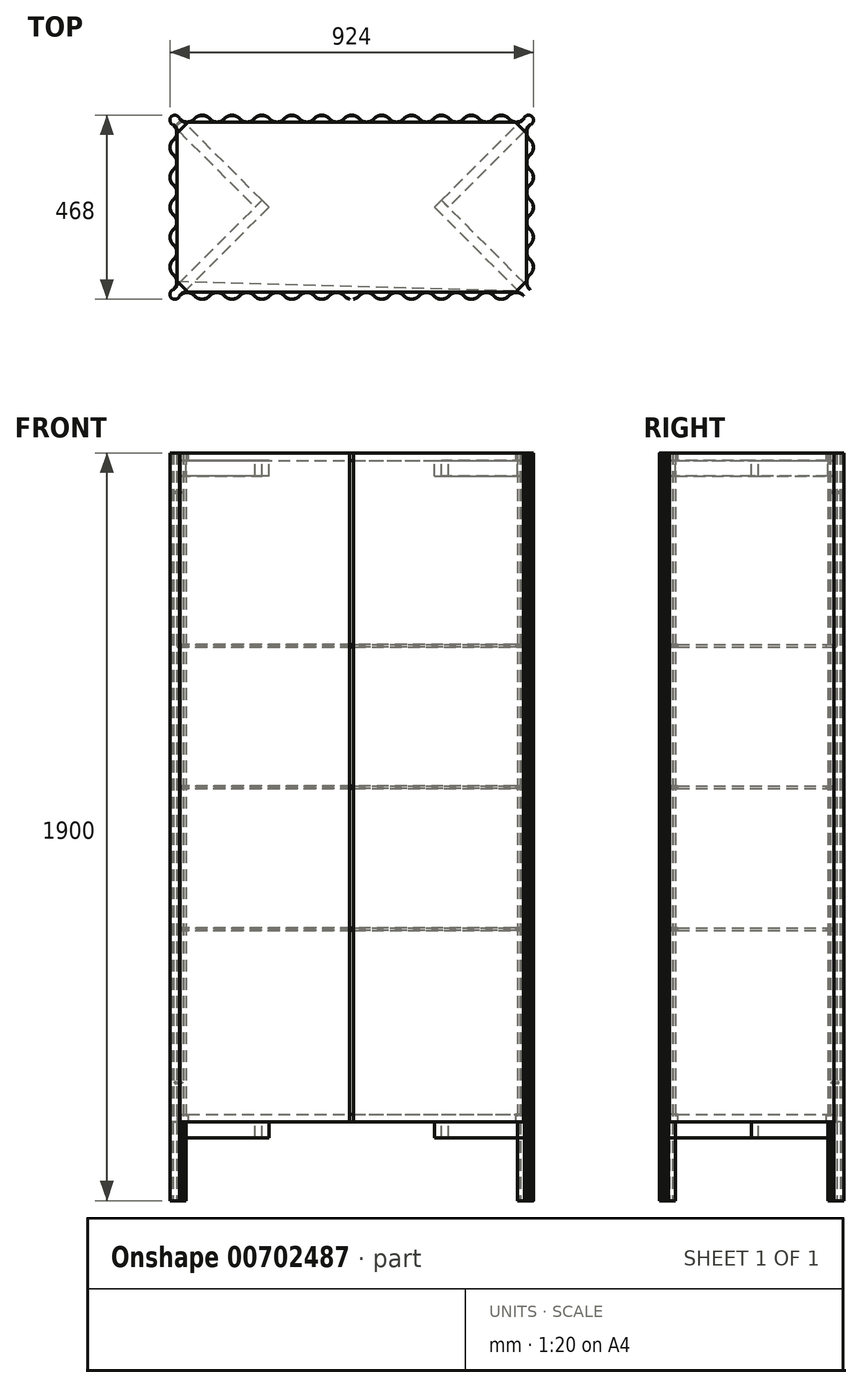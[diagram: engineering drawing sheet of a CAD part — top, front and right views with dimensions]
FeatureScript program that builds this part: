
annotation { "Feature Type Name" : "Feature", "Feature Type Description" : "" }
export const myFeature = defineFeature(function(context is Context, id is Id, definition is map)
    precondition{}
    {
        {
            var Q0;
            Q0=qCreatedBy(makeId("Top.planeOp"),FACE);
            var sketch = newSketch(context, id + "F0", { "sketchPlane" : qUnion([Q0])});
            skArc(sketch, "E0", {"start": v(19, 224.64) * mm, "mid": v(10.44, 231.03) * mm, "end": v(0, 233.3) * mm});
            skArc(sketch, "E1", {"start": v(19, 224.64) * mm, "mid": v(27.56, 218.26) * mm, "end": v(38, 216) * mm});
            skLineSegment(sketch, "E2", {"start": v(0, 285.6) * mm, "end": v(0, 208.1) * mm, "construction": true});
            skArc(sketch, "E3.1", {"start": v(19.53, 225.1) * mm, "mid": v(10.73, 231.66) * mm, "end": v(0, 234) * mm});
            skArc(sketch, "E3.2", {"start": v(19.53, 225.1) * mm, "mid": v(27.85, 218.9) * mm, "end": v(38, 216.7) * mm});
            skLineSegment(sketch, "E4", {"start": v(-82.64, 234) * mm, "end": v(38, 234) * mm, "construction": true});
            skLineSegment(sketch, "E5", {"start": v(-38, 216) * mm, "end": v(38, 216) * mm, "construction": true});
            skLineSegment(sketch, "E6", {"start": v(465.57, 237.57) * mm, "end": v(228, 0) * mm, "construction": true});
            skLineSegment(sketch, "E7.bottom", {"start": v(440.65, 230.33) * mm, "end": v(437.4, 227.07) * mm});
            skLineSegment(sketch, "E7.right", {"start": v(421.2, 210.88) * mm, "end": v(438.88, 193.2) * mm});
            skArc(sketch, "E8", {"start": v(458.33, 212.65) * mm, "mid": v(458.33, 230.33) * mm, "end": v(440.65, 230.33) * mm});
            skArc(sketch, "E9.1.0.0", {"start": v(95, 224.64) * mm, "mid": v(103.56, 218.26) * mm, "end": v(114, 216) * mm});
            skArc(sketch, "E9.1.0.1", {"start": v(57, 224.64) * mm, "mid": v(48.44, 218.26) * mm, "end": v(38, 216) * mm});
            skArc(sketch, "E9.1.0.2", {"start": v(56.47, 225.1) * mm, "mid": v(48.15, 218.9) * mm, "end": v(38, 216.7) * mm});
            skArc(sketch, "E9.1.0.3", {"start": v(95.53, 225.1) * mm, "mid": v(76, 234) * mm, "end": v(56.47, 225.1) * mm});
            skLineSegment(sketch, "E9.1.0.4", {"start": v(38, 216) * mm, "end": v(114, 216) * mm, "construction": true});
            skLineSegment(sketch, "E9.1.0.5", {"start": v(-6.64, 234) * mm, "end": v(114, 234) * mm, "construction": true});
            skArc(sketch, "E9.1.0.6", {"start": v(95.53, 225.1) * mm, "mid": v(103.85, 218.9) * mm, "end": v(114, 216.7) * mm});
            skArc(sketch, "E9.1.0.7", {"start": v(95, 224.64) * mm, "mid": v(76, 233.3) * mm, "end": v(57, 224.64) * mm});
            skArc(sketch, "E9.2.0.0", {"start": v(171, 224.64) * mm, "mid": v(179.56, 218.26) * mm, "end": v(190, 216) * mm});
            skArc(sketch, "E9.2.0.1", {"start": v(133, 224.64) * mm, "mid": v(124.44, 218.26) * mm, "end": v(114, 216) * mm});
            skArc(sketch, "E9.2.0.2", {"start": v(132.47, 225.1) * mm, "mid": v(124.15, 218.9) * mm, "end": v(114, 216.7) * mm});
            skArc(sketch, "E9.2.0.3", {"start": v(171.53, 225.1) * mm, "mid": v(152, 234) * mm, "end": v(132.47, 225.1) * mm});
            skLineSegment(sketch, "E9.2.0.4", {"start": v(114, 216) * mm, "end": v(190, 216) * mm, "construction": true});
            skLineSegment(sketch, "E9.2.0.5", {"start": v(69.36, 234) * mm, "end": v(190, 234) * mm, "construction": true});
            skArc(sketch, "E9.2.0.6", {"start": v(171.53, 225.1) * mm, "mid": v(179.85, 218.9) * mm, "end": v(190, 216.7) * mm});
            skArc(sketch, "E9.2.0.7", {"start": v(171, 224.64) * mm, "mid": v(152, 233.3) * mm, "end": v(133, 224.64) * mm});
            skArc(sketch, "E9.3.0.0", {"start": v(247, 224.64) * mm, "mid": v(255.56, 218.26) * mm, "end": v(266, 216) * mm});
            skArc(sketch, "E9.3.0.1", {"start": v(209, 224.64) * mm, "mid": v(200.44, 218.26) * mm, "end": v(190, 216) * mm});
            skArc(sketch, "E9.3.0.2", {"start": v(208.47, 225.1) * mm, "mid": v(200.15, 218.9) * mm, "end": v(190, 216.7) * mm});
            skArc(sketch, "E9.3.0.3", {"start": v(247.53, 225.1) * mm, "mid": v(228, 234) * mm, "end": v(208.47, 225.1) * mm});
            skLineSegment(sketch, "E9.3.0.4", {"start": v(190, 216) * mm, "end": v(266, 216) * mm, "construction": true});
            skLineSegment(sketch, "E9.3.0.5", {"start": v(145.36, 234) * mm, "end": v(266, 234) * mm, "construction": true});
            skArc(sketch, "E9.3.0.6", {"start": v(247.53, 225.1) * mm, "mid": v(255.85, 218.9) * mm, "end": v(266, 216.7) * mm});
            skArc(sketch, "E9.3.0.7", {"start": v(247, 224.64) * mm, "mid": v(228, 233.3) * mm, "end": v(209, 224.64) * mm});
            skArc(sketch, "E9.4.0.0", {"start": v(323, 224.64) * mm, "mid": v(331.56, 218.26) * mm, "end": v(342, 216) * mm});
            skArc(sketch, "E9.4.0.1", {"start": v(285, 224.64) * mm, "mid": v(276.44, 218.26) * mm, "end": v(266, 216) * mm});
            skArc(sketch, "E9.4.0.2", {"start": v(284.47, 225.1) * mm, "mid": v(276.15, 218.9) * mm, "end": v(266, 216.7) * mm});
            skArc(sketch, "E9.4.0.3", {"start": v(323.53, 225.1) * mm, "mid": v(304, 234) * mm, "end": v(284.47, 225.1) * mm});
            skLineSegment(sketch, "E9.4.0.4", {"start": v(266, 216) * mm, "end": v(342, 216) * mm, "construction": true});
            skLineSegment(sketch, "E9.4.0.5", {"start": v(221.36, 234) * mm, "end": v(342, 234) * mm, "construction": true});
            skArc(sketch, "E9.4.0.6", {"start": v(323.53, 225.1) * mm, "mid": v(331.85, 218.9) * mm, "end": v(342, 216.7) * mm});
            skArc(sketch, "E9.4.0.7", {"start": v(323, 224.64) * mm, "mid": v(304, 233.3) * mm, "end": v(285, 224.64) * mm});
            skArc(sketch, "E9.5.0.0", {"start": v(399, 224.64) * mm, "mid": v(407.56, 218.26) * mm, "end": v(418, 216) * mm});
            skArc(sketch, "E9.5.0.1", {"start": v(361, 224.64) * mm, "mid": v(352.44, 218.26) * mm, "end": v(342, 216) * mm});
            skArc(sketch, "E9.5.0.2", {"start": v(360.47, 225.1) * mm, "mid": v(352.15, 218.9) * mm, "end": v(342, 216.7) * mm});
            skArc(sketch, "E9.5.0.3", {"start": v(399.53, 225.1) * mm, "mid": v(380, 234) * mm, "end": v(360.47, 225.1) * mm});
            skLineSegment(sketch, "E9.5.0.4", {"start": v(342, 216) * mm, "end": v(418, 216) * mm, "construction": true});
            skLineSegment(sketch, "E9.5.0.5", {"start": v(297.36, 234) * mm, "end": v(418, 234) * mm, "construction": true});
            skArc(sketch, "E9.5.0.6", {"start": v(399.53, 225.1) * mm, "mid": v(407.85, 218.9) * mm, "end": v(418, 216.7) * mm});
            skArc(sketch, "E9.5.0.7", {"start": v(399, 224.64) * mm, "mid": v(380, 233.3) * mm, "end": v(361, 224.64) * mm});
            skArc(sketch, "E10.5.0.1", {"start": v(437, 224.64) * mm, "mid": v(428.44, 218.26) * mm, "end": v(418, 216) * mm});
            skArc(sketch, "E10.5.0.2", {"start": v(436.47, 225.1) * mm, "mid": v(428.15, 218.9) * mm, "end": v(418, 216.7) * mm});
            skLineSegment(sketch, "E11.MirrorCS", {"start": v(444, 114) * mm, "end": v(444, 190) * mm, "construction": true});
            skLineSegment(sketch, "E12", {"start": v(437.4, 227.07) * mm, "end": v(438.46, 226.01) * mm});
            skLineSegment(sketch, "E13", {"start": v(438.46, 226.01) * mm, "end": v(428.56, 216.11) * mm});
            skLineSegment(sketch, "E14", {"start": v(428.56, 216.11) * mm, "end": v(427.5, 217.17) * mm});
            skLineSegment(sketch, "E15.trimOffspring", {"start": v(427.5, 217.17) * mm, "end": v(421.2, 210.88) * mm});
            skLineSegment(sketch, "E16", {"start": v(0, 0) * mm, "end": v(0, 159.22) * mm, "construction": true});
            skLineSegment(sketch, "E17.MirrorCS", {"start": v(445.17, 199.5) * mm, "end": v(438.88, 193.2) * mm});
            skLineSegment(sketch, "E18.MirrorCS", {"start": v(444.11, 200.56) * mm, "end": v(445.17, 199.5) * mm});
            skLineSegment(sketch, "E19.MirrorCS", {"start": v(455.07, 209.4) * mm, "end": v(454.01, 210.46) * mm});
            skLineSegment(sketch, "E20.MirrorCS", {"start": v(454.01, 210.46) * mm, "end": v(444.11, 200.56) * mm});
            skLineSegment(sketch, "E21.MirrorCS", {"start": v(458.33, 212.65) * mm, "end": v(455.07, 209.4) * mm});
            skLineSegment(sketch, "E22", {"start": v(418, 216.7) * mm, "end": v(418, 241.18) * mm, "construction": true});
            skLineSegment(sketch, "E23", {"start": v(446.3, 206.86) * mm, "end": v(429, 224.16) * mm, "construction": true});
            skLineSegment(sketch, "E24", {"start": v(228, 0) * mm, "end": v(0, 0) * mm, "construction": true});
            skPoint(sketch, "E25", {"position": v(0, 234) * mm});
            skLineSegment(sketch, "E26.MirrorCS", {"start": v(444.7, 190) * mm, "end": v(469.18, 190) * mm, "construction": true});
            skArc(sketch, "E27.MirrorCS", {"start": v(452.64, 209) * mm, "mid": v(446.26, 200.44) * mm, "end": v(444, 190) * mm});
            skArc(sketch, "E28.MirrorCS", {"start": v(453.1, 208.47) * mm, "mid": v(446.9, 200.15) * mm, "end": v(444.7, 190) * mm});
            skArc(sketch, "E29.MirrorCS", {"start": v(453.1, 171.53) * mm, "mid": v(446.9, 179.85) * mm, "end": v(444.7, 190) * mm});
            skArc(sketch, "E30.MirrorCS", {"start": v(452.64, 171) * mm, "mid": v(446.26, 179.56) * mm, "end": v(444, 190) * mm});
            skLineSegment(sketch, "E31.MirrorCS", {"start": v(462, 69.36) * mm, "end": v(462, 190) * mm, "construction": true});
            skPoint(sketch, "E32.MirrorP", {"position": v(462, -228) * mm});
            skArc(sketch, "E33.MirrorCS", {"start": v(452.64, 19) * mm, "mid": v(446.26, 27.56) * mm, "end": v(444, 38) * mm});
            skArc(sketch, "E34.MirrorCS", {"start": v(452.64, 57) * mm, "mid": v(446.26, 48.44) * mm, "end": v(444, 38) * mm});
            skArc(sketch, "E35.MirrorCS", {"start": v(452.64, -19) * mm, "mid": v(446.26, -27.56) * mm, "end": v(444, -38) * mm});
            skArc(sketch, "E36.MirrorCS", {"start": v(452.64, -171) * mm, "mid": v(446.26, -179.56) * mm, "end": v(444, -190) * mm});
            skArc(sketch, "E37.MirrorCS", {"start": v(453.1, -95.53) * mm, "mid": v(446.9, -103.85) * mm, "end": v(444.7, -114) * mm});
            skLineSegment(sketch, "E38.MirrorCS", {"start": v(462, -234.64) * mm, "end": v(462, -114) * mm, "construction": true});
            skArc(sketch, "E39.MirrorCS", {"start": v(453.1, -132.47) * mm, "mid": v(446.9, -124.15) * mm, "end": v(444.7, -114) * mm});
            skArc(sketch, "E40.MirrorCS", {"start": v(453.1, -171.53) * mm, "mid": v(446.9, -179.85) * mm, "end": v(444.7, -190) * mm});
            skArc(sketch, "E41.MirrorCS", {"start": v(453.1, 56.47) * mm, "mid": v(446.9, 48.15) * mm, "end": v(444.7, 38) * mm});
            skArc(sketch, "E42.MirrorCS", {"start": v(453.1, 171.53) * mm, "mid": v(462, 152) * mm, "end": v(453.1, 132.47) * mm});
            skLineSegment(sketch, "E43.MirrorCS", {"start": v(462, -82.64) * mm, "end": v(462, 38) * mm, "construction": true});
            skArc(sketch, "E44.MirrorCS", {"start": v(452.64, -95) * mm, "mid": v(446.26, -103.56) * mm, "end": v(444, -114) * mm});
            skArc(sketch, "E45.MirrorCS", {"start": v(452.64, -57) * mm, "mid": v(461.3, -76) * mm, "end": v(452.64, -95) * mm});
            skLineSegment(sketch, "E46.MirrorCS", {"start": v(444, -114) * mm, "end": v(444, -38) * mm, "construction": true});
            skLineSegment(sketch, "E47.MirrorCS", {"start": v(444, 38) * mm, "end": v(444, 114) * mm, "construction": true});
            skLineSegment(sketch, "E48.MirrorCS", {"start": v(462, -158.64) * mm, "end": v(462, -38) * mm, "construction": true});
            skArc(sketch, "E49.MirrorCS", {"start": v(452.64, 133) * mm, "mid": v(446.26, 124.44) * mm, "end": v(444, 114) * mm});
            skLineSegment(sketch, "E50.MirrorCS", {"start": v(444, -38) * mm, "end": v(444, 38) * mm, "construction": true});
            skArc(sketch, "E51.MirrorCS", {"start": v(452.64, 95) * mm, "mid": v(446.26, 103.56) * mm, "end": v(444, 114) * mm});
            skArc(sketch, "E52.MirrorCS", {"start": v(453.1, 19.53) * mm, "mid": v(446.9, 27.85) * mm, "end": v(444.7, 38) * mm});
            skLineSegment(sketch, "E53.MirrorCS", {"start": v(462, -6.64) * mm, "end": v(462, 114) * mm, "construction": true});
            skLineSegment(sketch, "E54.MirrorCS", {"start": v(444, -190) * mm, "end": v(444, -114) * mm, "construction": true});
            skArc(sketch, "E55.MirrorCS", {"start": v(453.1, -132.47) * mm, "mid": v(462, -152) * mm, "end": v(453.1, -171.53) * mm});
            skArc(sketch, "E56.MirrorCS", {"start": v(452.64, 95) * mm, "mid": v(461.3, 76) * mm, "end": v(452.64, 57) * mm});
            skArc(sketch, "E57.MirrorCS", {"start": v(452.64, -57) * mm, "mid": v(446.26, -48.44) * mm, "end": v(444, -38) * mm});
            skArc(sketch, "E58.MirrorCS", {"start": v(452.64, 19) * mm, "mid": v(461.3, 0) * mm, "end": v(452.64, -19) * mm});
            skArc(sketch, "E59.MirrorCS", {"start": v(453.1, 19.53) * mm, "mid": v(462, 0) * mm, "end": v(453.1, -19.53) * mm});
            skArc(sketch, "E60.MirrorCS", {"start": v(453.1, -56.47) * mm, "mid": v(462, -76) * mm, "end": v(453.1, -95.53) * mm});
            skArc(sketch, "E61.MirrorCS", {"start": v(453.1, 95.53) * mm, "mid": v(446.9, 103.85) * mm, "end": v(444.7, 114) * mm});
            skArc(sketch, "E62.MirrorCS", {"start": v(452.64, -133) * mm, "mid": v(446.26, -124.44) * mm, "end": v(444, -114) * mm});
            skArc(sketch, "E63.MirrorCS", {"start": v(453.1, -19.53) * mm, "mid": v(446.9, -27.85) * mm, "end": v(444.7, -38) * mm});
            skArc(sketch, "E64.MirrorCS", {"start": v(452.64, -133) * mm, "mid": v(461.3, -152) * mm, "end": v(452.64, -171) * mm});
            skArc(sketch, "E65.MirrorCS", {"start": v(452.64, 171) * mm, "mid": v(461.3, 152) * mm, "end": v(452.64, 133) * mm});
            skArc(sketch, "E66.MirrorCS", {"start": v(453.1, 95.53) * mm, "mid": v(462, 76) * mm, "end": v(453.1, 56.47) * mm});
            skArc(sketch, "E67.MirrorCS", {"start": v(453.1, 132.47) * mm, "mid": v(446.9, 124.15) * mm, "end": v(444.7, 114) * mm});
            skArc(sketch, "E68.MirrorCS", {"start": v(453.1, -56.47) * mm, "mid": v(446.9, -48.15) * mm, "end": v(444.7, -38) * mm});
            skArc(sketch, "E69.MirrorCS", {"start": v(453.1, -208.47) * mm, "mid": v(446.9, -200.15) * mm, "end": v(444.7, -190) * mm});
            skArc(sketch, "E70.MirrorCS", {"start": v(452.64, -209) * mm, "mid": v(446.26, -200.44) * mm, "end": v(444, -190) * mm});
            skLineSegment(sketch, "E71.MirrorCS", {"start": v(444.11, -200.56) * mm, "end": v(445.17, -199.5) * mm});
            skLineSegment(sketch, "E72.MirrorCS", {"start": v(455.07, -209.4) * mm, "end": v(454.01, -210.46) * mm});
            skLineSegment(sketch, "E73.MirrorCS", {"start": v(421.2, -210.88) * mm, "end": v(438.88, -193.2) * mm});
            skArc(sketch, "E74.MirrorCS", {"start": v(458.33, -212.65) * mm, "mid": v(458.33, -230.33) * mm, "end": v(440.65, -230.33) * mm});
            skLineSegment(sketch, "E75.MirrorCS", {"start": v(445.17, -199.5) * mm, "end": v(438.88, -193.2) * mm});
            skLineSegment(sketch, "E76.MirrorCS", {"start": v(454.01, -210.46) * mm, "end": v(444.11, -200.56) * mm});
            skLineSegment(sketch, "E77.MirrorCS", {"start": v(458.33, -212.65) * mm, "end": v(455.07, -209.4) * mm});
            skLineSegment(sketch, "E78.MirrorCS", {"start": v(465.57, -237.57) * mm, "end": v(228, 0) * mm, "construction": true});
            skLineSegment(sketch, "E79.MirrorCS", {"start": v(446.3, -206.86) * mm, "end": v(429, -224.16) * mm, "construction": true});
            skArc(sketch, "E80.MirrorCS", {"start": v(436.47, -225.1) * mm, "mid": v(428.15, -218.9) * mm, "end": v(418, -216.7) * mm});
            skArc(sketch, "E81.MirrorCS", {"start": v(437, -224.64) * mm, "mid": v(428.44, -218.26) * mm, "end": v(418, -216) * mm});
            skArc(sketch, "E82.MirrorCS", {"start": v(19, -224.64) * mm, "mid": v(12.67, -229.87) * mm, "end": v(5, -232.8) * mm});
            skArc(sketch, "E83.MirrorCS", {"start": v(19.53, -225.1) * mm, "mid": v(12.96, -230.51) * mm, "end": v(5, -233.5) * mm});
            skArc(sketch, "E84.MirrorCS", {"start": v(323, -224.64) * mm, "mid": v(304, -233.3) * mm, "end": v(285, -224.64) * mm});
            skArc(sketch, "E85.MirrorCS", {"start": v(171, -224.64) * mm, "mid": v(152, -233.3) * mm, "end": v(133, -224.64) * mm});
            skArc(sketch, "E86.MirrorCS", {"start": v(171, -224.64) * mm, "mid": v(179.56, -218.26) * mm, "end": v(190, -216) * mm});
            skArc(sketch, "E87.MirrorCS", {"start": v(132.47, -225.1) * mm, "mid": v(124.15, -218.9) * mm, "end": v(114, -216.7) * mm});
            skArc(sketch, "E88.MirrorCS", {"start": v(323.53, -225.1) * mm, "mid": v(331.85, -218.9) * mm, "end": v(342, -216.7) * mm});
            skArc(sketch, "E89.MirrorCS", {"start": v(247, -224.64) * mm, "mid": v(255.56, -218.26) * mm, "end": v(266, -216) * mm});
            skArc(sketch, "E90.MirrorCS", {"start": v(171.53, -225.1) * mm, "mid": v(179.85, -218.9) * mm, "end": v(190, -216.7) * mm});
            skArc(sketch, "E91.MirrorCS", {"start": v(95, -224.64) * mm, "mid": v(76, -233.3) * mm, "end": v(57, -224.64) * mm});
            skArc(sketch, "E92.MirrorCS", {"start": v(399, -224.64) * mm, "mid": v(380, -233.3) * mm, "end": v(361, -224.64) * mm});
            skArc(sketch, "E93.MirrorCS", {"start": v(247, -224.64) * mm, "mid": v(228, -233.3) * mm, "end": v(209, -224.64) * mm});
            skArc(sketch, "E94.MirrorCS", {"start": v(95, -224.64) * mm, "mid": v(103.56, -218.26) * mm, "end": v(114, -216) * mm});
            skArc(sketch, "E95.MirrorCS", {"start": v(209, -224.64) * mm, "mid": v(200.44, -218.26) * mm, "end": v(190, -216) * mm});
            skArc(sketch, "E96.MirrorCS", {"start": v(361, -224.64) * mm, "mid": v(352.44, -218.26) * mm, "end": v(342, -216) * mm});
            skArc(sketch, "E97.MirrorCS", {"start": v(208.47, -225.1) * mm, "mid": v(200.15, -218.9) * mm, "end": v(190, -216.7) * mm});
            skArc(sketch, "E98.MirrorCS", {"start": v(360.47, -225.1) * mm, "mid": v(352.15, -218.9) * mm, "end": v(342, -216.7) * mm});
            skArc(sketch, "E99.MirrorCS", {"start": v(19, -224.64) * mm, "mid": v(27.56, -218.26) * mm, "end": v(38, -216) * mm});
            skArc(sketch, "E100.MirrorCS", {"start": v(399.53, -225.1) * mm, "mid": v(407.85, -218.9) * mm, "end": v(418, -216.7) * mm});
            skArc(sketch, "E101.MirrorCS", {"start": v(399, -224.64) * mm, "mid": v(407.56, -218.26) * mm, "end": v(418, -216) * mm});
            skArc(sketch, "E102.MirrorCS", {"start": v(57, -224.64) * mm, "mid": v(48.44, -218.26) * mm, "end": v(38, -216) * mm});
            skArc(sketch, "E103.MirrorCS", {"start": v(285, -224.64) * mm, "mid": v(276.44, -218.26) * mm, "end": v(266, -216) * mm});
            skArc(sketch, "E104.MirrorCS", {"start": v(133, -224.64) * mm, "mid": v(124.44, -218.26) * mm, "end": v(114, -216) * mm});
            skArc(sketch, "E105.MirrorCS", {"start": v(19.53, -225.1) * mm, "mid": v(27.85, -218.9) * mm, "end": v(38, -216.7) * mm});
            skArc(sketch, "E106.MirrorCS", {"start": v(171.53, -225.1) * mm, "mid": v(152, -234) * mm, "end": v(132.47, -225.1) * mm});
            skArc(sketch, "E107.MirrorCS", {"start": v(284.47, -225.1) * mm, "mid": v(276.15, -218.9) * mm, "end": v(266, -216.7) * mm});
            skArc(sketch, "E108.MirrorCS", {"start": v(56.47, -225.1) * mm, "mid": v(48.15, -218.9) * mm, "end": v(38, -216.7) * mm});
            skArc(sketch, "E109.MirrorCS", {"start": v(399.53, -225.1) * mm, "mid": v(380, -234) * mm, "end": v(360.47, -225.1) * mm});
            skArc(sketch, "E110.MirrorCS", {"start": v(95.53, -225.1) * mm, "mid": v(103.85, -218.9) * mm, "end": v(114, -216.7) * mm});
            skArc(sketch, "E111.MirrorCS", {"start": v(95.53, -225.1) * mm, "mid": v(76, -234) * mm, "end": v(56.47, -225.1) * mm});
            skArc(sketch, "E112.MirrorCS", {"start": v(323, -224.64) * mm, "mid": v(331.56, -218.26) * mm, "end": v(342, -216) * mm});
            skArc(sketch, "E113.MirrorCS", {"start": v(247.53, -225.1) * mm, "mid": v(228, -234) * mm, "end": v(208.47, -225.1) * mm});
            skArc(sketch, "E114.MirrorCS", {"start": v(247.53, -225.1) * mm, "mid": v(255.85, -218.9) * mm, "end": v(266, -216.7) * mm});
            skArc(sketch, "E115.MirrorCS", {"start": v(323.53, -225.1) * mm, "mid": v(304, -234) * mm, "end": v(284.47, -225.1) * mm});
            skLineSegment(sketch, "E116", {"start": v(437, 224.64) * mm, "end": v(436.47, 225.1) * mm});
            skLineSegment(sketch, "E117.MirrorCS", {"start": v(452.64, 209) * mm, "end": v(453.1, 208.47) * mm});
            skLineSegment(sketch, "E118.MirrorCS", {"start": v(452.64, -209) * mm, "end": v(453.1, -208.47) * mm});
            skLineSegment(sketch, "E119.MirrorCS", {"start": v(437, -224.64) * mm, "end": v(436.47, -225.1) * mm});
            skLineSegment(sketch, "E120", {"start": v(5, -232.8) * mm, "end": v(5, -233.5) * mm});
            skLineSegment(sketch, "E121.MirrorCS", {"start": v(-452.64, 209) * mm, "end": v(-453.1, 208.47) * mm});
            skLineSegment(sketch, "E122.MirrorCS", {"start": v(-455.07, 209.4) * mm, "end": v(-454.01, 210.46) * mm});
            skLineSegment(sketch, "E123.MirrorCS", {"start": v(-444.11, 200.56) * mm, "end": v(-445.17, 199.5) * mm});
            skLineSegment(sketch, "E124.MirrorCS", {"start": v(-437, 224.64) * mm, "end": v(-436.47, 225.1) * mm});
            skLineSegment(sketch, "E125.MirrorCS", {"start": v(-437.4, 227.07) * mm, "end": v(-438.46, 226.01) * mm});
            skLineSegment(sketch, "E126.MirrorCS", {"start": v(-438.46, 226.01) * mm, "end": v(-428.56, 216.11) * mm});
            skLineSegment(sketch, "E127.MirrorCS", {"start": v(-458.33, 212.65) * mm, "end": v(-455.07, 209.4) * mm});
            skArc(sketch, "E128.MirrorCS", {"start": v(-437, 224.64) * mm, "mid": v(-428.44, 218.26) * mm, "end": v(-418, 216) * mm});
            skLineSegment(sketch, "E129.MirrorCS", {"start": v(-454.01, 210.46) * mm, "end": v(-444.11, 200.56) * mm});
            skArc(sketch, "E130.MirrorCS", {"start": v(-452.64, 209) * mm, "mid": v(-446.26, 200.44) * mm, "end": v(-444, 190) * mm});
            skLineSegment(sketch, "E131.MirrorCS", {"start": v(-428.56, 216.11) * mm, "end": v(-427.5, 217.17) * mm});
            skLineSegment(sketch, "E132.MirrorCS", {"start": v(-427.5, 217.17) * mm, "end": v(-421.2, 210.88) * mm});
            skLineSegment(sketch, "E133.MirrorCS", {"start": v(-446.3, 206.86) * mm, "end": v(-429, 224.16) * mm, "construction": true});
            skArc(sketch, "E134.MirrorCS", {"start": v(-453.1, 208.47) * mm, "mid": v(-446.9, 200.15) * mm, "end": v(-444.7, 190) * mm});
            skArc(sketch, "E135.MirrorCS", {"start": v(-436.47, 225.1) * mm, "mid": v(-428.15, 218.9) * mm, "end": v(-418, 216.7) * mm});
            skLineSegment(sketch, "E136.MirrorCS", {"start": v(-440.65, 230.33) * mm, "end": v(-437.4, 227.07) * mm});
            skLineSegment(sketch, "E137.MirrorCS", {"start": v(-445.17, 199.5) * mm, "end": v(-438.88, 193.2) * mm});
            skLineSegment(sketch, "E138.MirrorCS", {"start": v(-452.64, -209) * mm, "end": v(-453.1, -208.47) * mm});
            skLineSegment(sketch, "E139.MirrorCS", {"start": v(-418, 216.7) * mm, "end": v(-418, 241.18) * mm, "construction": true});
            skLineSegment(sketch, "E140.MirrorCS", {"start": v(-455.07, -209.4) * mm, "end": v(-454.01, -210.46) * mm});
            skLineSegment(sketch, "E141.MirrorCS", {"start": v(-444.11, -200.56) * mm, "end": v(-445.17, -199.5) * mm});
            skLineSegment(sketch, "E142.MirrorCS", {"start": v(-437.4, -227.07) * mm, "end": v(-438.46, -226.01) * mm});
            skLineSegment(sketch, "E143.MirrorCS", {"start": v(-444.7, 190) * mm, "end": v(-469.18, 190) * mm, "construction": true});
            skLineSegment(sketch, "E144.MirrorCS", {"start": v(-440.65, -230.33) * mm, "end": v(-437.4, -227.07) * mm});
            skLineSegment(sketch, "E145.MirrorCS", {"start": v(-437, -224.64) * mm, "end": v(-436.47, -225.1) * mm});
            skArc(sketch, "E146.MirrorCS", {"start": v(-452.64, -209) * mm, "mid": v(-446.26, -200.44) * mm, "end": v(-444, -190) * mm});
            skArc(sketch, "E147.MirrorCS", {"start": v(-453.1, -208.47) * mm, "mid": v(-446.9, -200.15) * mm, "end": v(-444.7, -190) * mm});
            skLineSegment(sketch, "E148.MirrorCS", {"start": v(-438.46, -226.01) * mm, "end": v(-428.56, -216.11) * mm});
            skLineSegment(sketch, "E149.MirrorCS", {"start": v(-446.3, -206.86) * mm, "end": v(-429, -224.16) * mm, "construction": true});
            skLineSegment(sketch, "E150.MirrorCS", {"start": v(-445.17, -199.5) * mm, "end": v(-438.88, -193.2) * mm});
            skArc(sketch, "E151.MirrorCS", {"start": v(-19.53, -225.1) * mm, "mid": v(-12.96, -230.51) * mm, "end": v(-5, -233.5) * mm});
            skLineSegment(sketch, "E152.MirrorCS", {"start": v(-428.56, -216.11) * mm, "end": v(-427.5, -217.17) * mm});
            skArc(sketch, "E153.MirrorCS", {"start": v(-95, 224.64) * mm, "mid": v(-103.56, 218.26) * mm, "end": v(-114, 216) * mm});
            skLineSegment(sketch, "E154.MirrorCS", {"start": v(-454.01, -210.46) * mm, "end": v(-444.11, -200.56) * mm});
            skLineSegment(sketch, "E155.MirrorCS", {"start": v(-458.33, -212.65) * mm, "end": v(-455.07, -209.4) * mm});
            skLineSegment(sketch, "E156.MirrorCS", {"start": v(-5, -232.8) * mm, "end": v(-5, -233.5) * mm});
            skArc(sketch, "E157.MirrorCS", {"start": v(-399, 224.64) * mm, "mid": v(-407.56, 218.26) * mm, "end": v(-418, 216) * mm});
            skArc(sketch, "E158.MirrorCS", {"start": v(-19, 224.64) * mm, "mid": v(-27.56, 218.26) * mm, "end": v(-38, 216) * mm});
            skArc(sketch, "E159.MirrorCS", {"start": v(-95.53, 225.1) * mm, "mid": v(-103.85, 218.9) * mm, "end": v(-114, 216.7) * mm});
            skArc(sketch, "E160.MirrorCS", {"start": v(-437, -224.64) * mm, "mid": v(-428.44, -218.26) * mm, "end": v(-418, -216) * mm});
            skArc(sketch, "E161.MirrorCS", {"start": v(-453.1, -171.53) * mm, "mid": v(-446.9, -179.85) * mm, "end": v(-444.7, -190) * mm});
            skArc(sketch, "E162.MirrorCS", {"start": v(-453.1, 171.53) * mm, "mid": v(-446.9, 179.85) * mm, "end": v(-444.7, 190) * mm});
            skArc(sketch, "E163.MirrorCS", {"start": v(-452.64, 133) * mm, "mid": v(-446.26, 124.44) * mm, "end": v(-444, 114) * mm});
            skArc(sketch, "E164.MirrorCS", {"start": v(-19, -224.64) * mm, "mid": v(-12.67, -229.87) * mm, "end": v(-5, -232.8) * mm});
            skArc(sketch, "E165.MirrorCS", {"start": v(-453.1, 56.47) * mm, "mid": v(-446.9, 48.15) * mm, "end": v(-444.7, 38) * mm});
            skArc(sketch, "E166.MirrorCS", {"start": v(-133, 224.64) * mm, "mid": v(-124.44, 218.26) * mm, "end": v(-114, 216) * mm});
            skArc(sketch, "E167.MirrorCS", {"start": v(-19, -224.64) * mm, "mid": v(-27.56, -218.26) * mm, "end": v(-38, -216) * mm});
            skArc(sketch, "E168.MirrorCS", {"start": v(-285, -224.64) * mm, "mid": v(-276.44, -218.26) * mm, "end": v(-266, -216) * mm});
            skArc(sketch, "E169.MirrorCS", {"start": v(-453.1, 95.53) * mm, "mid": v(-446.9, 103.85) * mm, "end": v(-444.7, 114) * mm});
            skArc(sketch, "E170.MirrorCS", {"start": v(-399.53, 225.1) * mm, "mid": v(-407.85, 218.9) * mm, "end": v(-418, 216.7) * mm});
            skArc(sketch, "E171.MirrorCS", {"start": v(-285, 224.64) * mm, "mid": v(-276.44, 218.26) * mm, "end": v(-266, 216) * mm});
            skArc(sketch, "E172.MirrorCS", {"start": v(-247, -224.64) * mm, "mid": v(-255.56, -218.26) * mm, "end": v(-266, -216) * mm});
            skArc(sketch, "E173.MirrorCS", {"start": v(-19.53, -225.1) * mm, "mid": v(-27.85, -218.9) * mm, "end": v(-38, -216.7) * mm});
            skArc(sketch, "E174.MirrorCS", {"start": v(-452.64, 171) * mm, "mid": v(-446.26, 179.56) * mm, "end": v(-444, 190) * mm});
            skArc(sketch, "E175.MirrorCS", {"start": v(-452.64, -133) * mm, "mid": v(-446.26, -124.44) * mm, "end": v(-444, -114) * mm});
            skArc(sketch, "E176.MirrorCS", {"start": v(-57, 224.64) * mm, "mid": v(-48.44, 218.26) * mm, "end": v(-38, 216) * mm});
            skArc(sketch, "E177.MirrorCS", {"start": v(-453.1, -132.47) * mm, "mid": v(-446.9, -124.15) * mm, "end": v(-444.7, -114) * mm});
            skArc(sketch, "E178.MirrorCS", {"start": v(-95.53, -225.1) * mm, "mid": v(-103.85, -218.9) * mm, "end": v(-114, -216.7) * mm});
            skArc(sketch, "E179.MirrorCS", {"start": v(-453.1, -19.53) * mm, "mid": v(-446.9, -27.85) * mm, "end": v(-444.7, -38) * mm});
            skArc(sketch, "E180.MirrorCS", {"start": v(-171.53, -225.1) * mm, "mid": v(-179.85, -218.9) * mm, "end": v(-190, -216.7) * mm});
            skArc(sketch, "E181.MirrorCS", {"start": v(-171.53, 225.1) * mm, "mid": v(-179.85, 218.9) * mm, "end": v(-190, 216.7) * mm});
            skArc(sketch, "E182.MirrorCS", {"start": v(-452.64, 95) * mm, "mid": v(-446.26, 103.56) * mm, "end": v(-444, 114) * mm});
            skArc(sketch, "E183.MirrorCS", {"start": v(-56.47, 225.1) * mm, "mid": v(-48.15, 218.9) * mm, "end": v(-38, 216.7) * mm});
            skArc(sketch, "E184.MirrorCS", {"start": v(-133, -224.64) * mm, "mid": v(-124.44, -218.26) * mm, "end": v(-114, -216) * mm});
            skArc(sketch, "E185.MirrorCS", {"start": v(-208.47, -225.1) * mm, "mid": v(-200.15, -218.9) * mm, "end": v(-190, -216.7) * mm});
            skArc(sketch, "E186.MirrorCS", {"start": v(-19.53, 225.1) * mm, "mid": v(-27.85, 218.9) * mm, "end": v(-38, 216.7) * mm});
            skArc(sketch, "E187.MirrorCS", {"start": v(-453.1, 132.47) * mm, "mid": v(-446.9, 124.15) * mm, "end": v(-444.7, 114) * mm});
            skArc(sketch, "E188.MirrorCS", {"start": v(-247.53, 225.1) * mm, "mid": v(-255.85, 218.9) * mm, "end": v(-266, 216.7) * mm});
            skArc(sketch, "E189.MirrorCS", {"start": v(-247.53, -225.1) * mm, "mid": v(-255.85, -218.9) * mm, "end": v(-266, -216.7) * mm});
            skArc(sketch, "E190.MirrorCS", {"start": v(-208.47, 225.1) * mm, "mid": v(-200.15, 218.9) * mm, "end": v(-190, 216.7) * mm});
            skArc(sketch, "E191.MirrorCS", {"start": v(-284.47, 225.1) * mm, "mid": v(-276.15, 218.9) * mm, "end": v(-266, 216.7) * mm});
            skArc(sketch, "E192.MirrorCS", {"start": v(-436.47, -225.1) * mm, "mid": v(-428.15, -218.9) * mm, "end": v(-418, -216.7) * mm});
            skArc(sketch, "E193.MirrorCS", {"start": v(-453.1, 19.53) * mm, "mid": v(-446.9, 27.85) * mm, "end": v(-444.7, 38) * mm});
            skArc(sketch, "E194.MirrorCS", {"start": v(-132.47, -225.1) * mm, "mid": v(-124.15, -218.9) * mm, "end": v(-114, -216.7) * mm});
            skArc(sketch, "E195.MirrorCS", {"start": v(-399, -224.64) * mm, "mid": v(-407.56, -218.26) * mm, "end": v(-418, -216) * mm});
            skArc(sketch, "E196.MirrorCS", {"start": v(-452.64, -19) * mm, "mid": v(-446.26, -27.56) * mm, "end": v(-444, -38) * mm});
            skArc(sketch, "E197.MirrorCS", {"start": v(-209, -224.64) * mm, "mid": v(-200.44, -218.26) * mm, "end": v(-190, -216) * mm});
            skArc(sketch, "E198.MirrorCS", {"start": v(-171, 224.64) * mm, "mid": v(-179.56, 218.26) * mm, "end": v(-190, 216) * mm});
            skArc(sketch, "E199.MirrorCS", {"start": v(-399.53, -225.1) * mm, "mid": v(-407.85, -218.9) * mm, "end": v(-418, -216.7) * mm});
            skArc(sketch, "E200.MirrorCS", {"start": v(-56.47, -225.1) * mm, "mid": v(-48.15, -218.9) * mm, "end": v(-38, -216.7) * mm});
            skArc(sketch, "E201.MirrorCS", {"start": v(-452.64, -95) * mm, "mid": v(-446.26, -103.56) * mm, "end": v(-444, -114) * mm});
            skArc(sketch, "E202.MirrorCS", {"start": v(-247, 224.64) * mm, "mid": v(-255.56, 218.26) * mm, "end": v(-266, 216) * mm});
            skArc(sketch, "E203.MirrorCS", {"start": v(-452.64, 57) * mm, "mid": v(-446.26, 48.44) * mm, "end": v(-444, 38) * mm});
            skArc(sketch, "E204.MirrorCS", {"start": v(-361, 224.64) * mm, "mid": v(-352.44, 218.26) * mm, "end": v(-342, 216) * mm});
            skArc(sketch, "E205.MirrorCS", {"start": v(-453.1, -95.53) * mm, "mid": v(-446.9, -103.85) * mm, "end": v(-444.7, -114) * mm});
            skArc(sketch, "E206.MirrorCS", {"start": v(-452.64, -57) * mm, "mid": v(-446.26, -48.44) * mm, "end": v(-444, -38) * mm});
            skArc(sketch, "E207.MirrorCS", {"start": v(-453.1, -56.47) * mm, "mid": v(-446.9, -48.15) * mm, "end": v(-444.7, -38) * mm});
            skArc(sketch, "E208.MirrorCS", {"start": v(-452.64, 19) * mm, "mid": v(-446.26, 27.56) * mm, "end": v(-444, 38) * mm});
            skArc(sketch, "E209.MirrorCS", {"start": v(-361, -224.64) * mm, "mid": v(-352.44, -218.26) * mm, "end": v(-342, -216) * mm});
            skArc(sketch, "E210.MirrorCS", {"start": v(-132.47, 225.1) * mm, "mid": v(-124.15, 218.9) * mm, "end": v(-114, 216.7) * mm});
            skArc(sketch, "E211.MirrorCS", {"start": v(-171, -224.64) * mm, "mid": v(-179.56, -218.26) * mm, "end": v(-190, -216) * mm});
            skArc(sketch, "E212.MirrorCS", {"start": v(-57, -224.64) * mm, "mid": v(-48.44, -218.26) * mm, "end": v(-38, -216) * mm});
            skArc(sketch, "E213.MirrorCS", {"start": v(-95, -224.64) * mm, "mid": v(-103.56, -218.26) * mm, "end": v(-114, -216) * mm});
            skArc(sketch, "E214.MirrorCS", {"start": v(-209, 224.64) * mm, "mid": v(-200.44, 218.26) * mm, "end": v(-190, 216) * mm});
            skArc(sketch, "E215.MirrorCS", {"start": v(-452.64, -171) * mm, "mid": v(-446.26, -179.56) * mm, "end": v(-444, -190) * mm});
            skLineSegment(sketch, "E216.MirrorCS", {"start": v(-427.5, -217.17) * mm, "end": v(-421.2, -210.88) * mm});
            skArc(sketch, "E217.MirrorCS", {"start": v(-284.47, -225.1) * mm, "mid": v(-276.15, -218.9) * mm, "end": v(-266, -216.7) * mm});
            skArc(sketch, "E218.MirrorCS", {"start": v(-360.47, 225.1) * mm, "mid": v(-352.15, 218.9) * mm, "end": v(-342, 216.7) * mm});
            skArc(sketch, "E219.MirrorCS", {"start": v(-323, -224.64) * mm, "mid": v(-331.56, -218.26) * mm, "end": v(-342, -216) * mm});
            skArc(sketch, "E220.MirrorCS", {"start": v(-323.53, 225.1) * mm, "mid": v(-331.85, 218.9) * mm, "end": v(-342, 216.7) * mm});
            skArc(sketch, "E221.MirrorCS", {"start": v(-323.53, -225.1) * mm, "mid": v(-331.85, -218.9) * mm, "end": v(-342, -216.7) * mm});
            skArc(sketch, "E222.MirrorCS", {"start": v(-19.53, 225.1) * mm, "mid": v(-10.73, 231.66) * mm, "end": v(0, 234) * mm});
            skLineSegment(sketch, "E223.MirrorCS", {"start": v(-38, 216) * mm, "end": v(-114, 216) * mm, "construction": true});
            skArc(sketch, "E224.MirrorCS", {"start": v(-19, 224.64) * mm, "mid": v(-10.44, 231.03) * mm, "end": v(0, 233.3) * mm});
            skArc(sketch, "E225.MirrorCS", {"start": v(-458.33, 212.65) * mm, "mid": v(-458.33, 230.33) * mm, "end": v(-440.65, 230.33) * mm});
            skArc(sketch, "E226.MirrorCS", {"start": v(-323, 224.64) * mm, "mid": v(-331.56, 218.26) * mm, "end": v(-342, 216) * mm});
            skArc(sketch, "E227.MirrorCS", {"start": v(-360.47, -225.1) * mm, "mid": v(-352.15, -218.9) * mm, "end": v(-342, -216.7) * mm});
            skLineSegment(sketch, "E228.MirrorCS", {"start": v(-421.2, 210.88) * mm, "end": v(-438.88, 193.2) * mm});
            skLineSegment(sketch, "E229.MirrorCS", {"start": v(-444, 114) * mm, "end": v(-444, 190) * mm, "construction": true});
            skLineSegment(sketch, "E230.MirrorCS", {"start": v(-444, -114) * mm, "end": v(-444, -38) * mm, "construction": true});
            skArc(sketch, "E231.MirrorCS", {"start": v(-458.33, -212.65) * mm, "mid": v(-458.33, -230.33) * mm, "end": v(-440.65, -230.33) * mm});
            skLineSegment(sketch, "E232.MirrorCS", {"start": v(-69.36, 234) * mm, "end": v(-190, 234) * mm, "construction": true});
            skLineSegment(sketch, "E233.MirrorCS", {"start": v(-221.36, 234) * mm, "end": v(-342, 234) * mm, "construction": true});
            skLineSegment(sketch, "E234.MirrorCS", {"start": v(-444, 38) * mm, "end": v(-444, 114) * mm, "construction": true});
            skLineSegment(sketch, "E235.MirrorCS", {"start": v(-462, -82.64) * mm, "end": v(-462, 38) * mm, "construction": true});
            skLineSegment(sketch, "E236.MirrorCS", {"start": v(-444, -190) * mm, "end": v(-444, -114) * mm, "construction": true});
            skLineSegment(sketch, "E237.MirrorCS", {"start": v(-297.36, 234) * mm, "end": v(-418, 234) * mm, "construction": true});
            skLineSegment(sketch, "E238.MirrorCS", {"start": v(6.64, 234) * mm, "end": v(-114, 234) * mm, "construction": true});
            skLineSegment(sketch, "E239.MirrorCS", {"start": v(-342, 216) * mm, "end": v(-418, 216) * mm, "construction": true});
            skArc(sketch, "E240.MirrorCS", {"start": v(-453.1, -56.47) * mm, "mid": v(-462, -76) * mm, "end": v(-453.1, -95.53) * mm});
            skLineSegment(sketch, "E241.MirrorCS", {"start": v(-421.2, -210.88) * mm, "end": v(-438.88, -193.2) * mm});
            skLineSegment(sketch, "E242.MirrorCS", {"start": v(-114, 216) * mm, "end": v(-190, 216) * mm, "construction": true});
            skLineSegment(sketch, "E243.MirrorCS", {"start": v(-266, 216) * mm, "end": v(-342, 216) * mm, "construction": true});
            skLineSegment(sketch, "E244.MirrorCS", {"start": v(-190, 216) * mm, "end": v(-266, 216) * mm, "construction": true});
            skLineSegment(sketch, "E245.MirrorCS", {"start": v(-444, -38) * mm, "end": v(-444, 38) * mm, "construction": true});
            skArc(sketch, "E246.MirrorCS", {"start": v(-171, 224.64) * mm, "mid": v(-152, 233.3) * mm, "end": v(-133, 224.64) * mm});
            skArc(sketch, "E247.MirrorCS", {"start": v(-453.1, 19.53) * mm, "mid": v(-462, 0) * mm, "end": v(-453.1, -19.53) * mm});
            skArc(sketch, "E248.MirrorCS", {"start": v(-95, 224.64) * mm, "mid": v(-76, 233.3) * mm, "end": v(-57, 224.64) * mm});
            skArc(sketch, "E249.MirrorCS", {"start": v(-95.53, 225.1) * mm, "mid": v(-76, 234) * mm, "end": v(-56.47, 225.1) * mm});
            skArc(sketch, "E250.MirrorCS", {"start": v(-452.64, -57) * mm, "mid": v(-461.3, -76) * mm, "end": v(-452.64, -95) * mm});
            skArc(sketch, "E251.MirrorCS", {"start": v(-399, 224.64) * mm, "mid": v(-380, 233.3) * mm, "end": v(-361, 224.64) * mm});
            skLineSegment(sketch, "E252.MirrorCS", {"start": v(-145.36, 234) * mm, "end": v(-266, 234) * mm, "construction": true});
            skLineSegment(sketch, "E253.MirrorCS", {"start": v(-462, -234.64) * mm, "end": v(-462, -114) * mm, "construction": true});
            skArc(sketch, "E254.MirrorCS", {"start": v(-452.64, 19) * mm, "mid": v(-461.3, 0) * mm, "end": v(-452.64, -19) * mm});
            skArc(sketch, "E255.MirrorCS", {"start": v(-452.64, 95) * mm, "mid": v(-461.3, 76) * mm, "end": v(-452.64, 57) * mm});
            skArc(sketch, "E256.MirrorCS", {"start": v(-399.53, 225.1) * mm, "mid": v(-380, 234) * mm, "end": v(-360.47, 225.1) * mm});
            skLineSegment(sketch, "E257.MirrorCS", {"start": v(-462, -158.64) * mm, "end": v(-462, -38) * mm, "construction": true});
            skArc(sketch, "E258.MirrorCS", {"start": v(-171.53, 225.1) * mm, "mid": v(-152, 234) * mm, "end": v(-132.47, 225.1) * mm});
            skArc(sketch, "E259.MirrorCS", {"start": v(-323.53, 225.1) * mm, "mid": v(-304, 234) * mm, "end": v(-284.47, 225.1) * mm});
            skArc(sketch, "E260.MirrorCS", {"start": v(-247.53, 225.1) * mm, "mid": v(-228, 234) * mm, "end": v(-208.47, 225.1) * mm});
            skArc(sketch, "E261.MirrorCS", {"start": v(-453.1, -132.47) * mm, "mid": v(-462, -152) * mm, "end": v(-453.1, -171.53) * mm});
            skArc(sketch, "E262.MirrorCS", {"start": v(-453.1, 95.53) * mm, "mid": v(-462, 76) * mm, "end": v(-453.1, 56.47) * mm});
            skArc(sketch, "E263.MirrorCS", {"start": v(-247, -224.64) * mm, "mid": v(-228, -233.3) * mm, "end": v(-209, -224.64) * mm});
            skLineSegment(sketch, "E264.MirrorCS", {"start": v(38, 216) * mm, "end": v(-38, 216) * mm, "construction": true});
            skArc(sketch, "E265.MirrorCS", {"start": v(-453.1, 171.53) * mm, "mid": v(-462, 152) * mm, "end": v(-453.1, 132.47) * mm});
            skArc(sketch, "E266.MirrorCS", {"start": v(-247, 224.64) * mm, "mid": v(-228, 233.3) * mm, "end": v(-209, 224.64) * mm});
            skArc(sketch, "E267.MirrorCS", {"start": v(-323, 224.64) * mm, "mid": v(-304, 233.3) * mm, "end": v(-285, 224.64) * mm});
            skLineSegment(sketch, "E268.MirrorCS", {"start": v(-462, -6.64) * mm, "end": v(-462, 114) * mm, "construction": true});
            skArc(sketch, "E269.MirrorCS", {"start": v(-452.64, -133) * mm, "mid": v(-461.3, -152) * mm, "end": v(-452.64, -171) * mm});
            skPoint(sketch, "E270.MirrorP", {"position": v(-462, -228) * mm});
            skArc(sketch, "E271.MirrorCS", {"start": v(-95.53, -225.1) * mm, "mid": v(-76, -234) * mm, "end": v(-56.47, -225.1) * mm});
            skArc(sketch, "E272.MirrorCS", {"start": v(-171, -224.64) * mm, "mid": v(-152, -233.3) * mm, "end": v(-133, -224.64) * mm});
            skArc(sketch, "E273.MirrorCS", {"start": v(-323.53, -225.1) * mm, "mid": v(-304, -234) * mm, "end": v(-284.47, -225.1) * mm});
            skArc(sketch, "E274.MirrorCS", {"start": v(-171.53, -225.1) * mm, "mid": v(-152, -234) * mm, "end": v(-132.47, -225.1) * mm});
            skLineSegment(sketch, "E275.MirrorCS", {"start": v(-462, 69.36) * mm, "end": v(-462, 190) * mm, "construction": true});
            skArc(sketch, "E276.MirrorCS", {"start": v(-95, -224.64) * mm, "mid": v(-76, -233.3) * mm, "end": v(-57, -224.64) * mm});
            skLineSegment(sketch, "E277.MirrorCS", {"start": v(82.64, 234) * mm, "end": v(-38, 234) * mm, "construction": true});
            skLineSegment(sketch, "E278.MirrorCS", {"start": v(-465.57, -237.57) * mm, "end": v(-228, 0) * mm, "construction": true});
            skArc(sketch, "E279.MirrorCS", {"start": v(-247.53, -225.1) * mm, "mid": v(-228, -234) * mm, "end": v(-208.47, -225.1) * mm});
            skArc(sketch, "E280.MirrorCS", {"start": v(-399.53, -225.1) * mm, "mid": v(-380, -234) * mm, "end": v(-360.47, -225.1) * mm});
            skArc(sketch, "E281.MirrorCS", {"start": v(-399, -224.64) * mm, "mid": v(-380, -233.3) * mm, "end": v(-361, -224.64) * mm});
            skArc(sketch, "E282.MirrorCS", {"start": v(-452.64, 171) * mm, "mid": v(-461.3, 152) * mm, "end": v(-452.64, 133) * mm});
            skArc(sketch, "E283.MirrorCS", {"start": v(-323, -224.64) * mm, "mid": v(-304, -233.3) * mm, "end": v(-285, -224.64) * mm});
            skLineSegment(sketch, "E284.MirrorCS", {"start": v(-465.57, 237.57) * mm, "end": v(-228, 0) * mm, "construction": true});
            skLineSegment(sketch, "E285.MirrorCS", {"start": v(-228, 0) * mm, "end": v(0, 0) * mm, "construction": true});
            skLineSegment(sketch, "E286", {"start": v(439.87, -224.6) * mm, "end": v(427.14, -211.87) * mm});
            skLineSegment(sketch, "E287", {"start": v(439.87, -224.6) * mm, "end": v(437.4, -227.07) * mm});
            skLineSegment(sketch, "E288", {"start": v(440.65, -230.33) * mm, "end": v(437.4, -227.07) * mm});
            skLineSegment(sketch, "E289", {"start": v(427.14, -211.87) * mm, "end": v(424.67, -214.35) * mm});
            skLineSegment(sketch, "E290", {"start": v(424.67, -214.35) * mm, "end": v(421.2, -210.88) * mm});
            skSolve(sketch);
        }
        {
            var Q0;
            {var subQ7=sQuery(id+"F0.wireOp",EDGE,"E140.MirrorCS");Q0=makeQuery(id+"F0.imprint","IMPRINT",FACE,{"disambiguationData":[TD([[makeQuery(id+"F0.imprint","IMPRINT",EDGE,{"derivedFrom":subQ7}),-1.0]])]});}
            var Q1;
            {var subQ4=sQuery(id+"F0.wireOp",EDGE,"E122.MirrorCS");Q1=makeQuery(id+"F0.imprint","IMPRINT",FACE,{"disambiguationData":[TD([[makeQuery(id+"F0.imprint","IMPRINT",EDGE,{"derivedFrom":subQ4}),1.0]])]});}
            var Q2;
            Q2=makeQuery(id+"F0.imprint","IMPRINT",FACE,{"disambiguationData":[TD([[makeQuery(id+"F0.imprint","IMPRINT",EDGE,{"derivedFrom":sQuery(id+"F0.wireOp",EDGE,"E7.bottom")}),1.0]])]});
            var Q3;
            {var subQ2=sQuery(id+"F0.wireOp",EDGE,"74604fba-330f-4715-a284-1bb773bec2d21.MirrorCS");Q3=makeQuery(id+"F0.imprint","IMPRINT",FACE,{"disambiguationData":[TD([[makeQuery(id+"F0.imprint","IMPRINT",EDGE,{"derivedFrom":subQ2}),-1.0]])]});}
            extrude(context, id + "F1", {"entities" : qUnion([Q0, Q1, Q2, Q3]), "depth" : 1700 * mm, "offsetDistance" : 25 * mm, "hasSecondDirection" : true, "secondDirectionOppositeDirection" : true, "secondDirectionDepth" : 200 * mm});
        }
        {
            var Q0;
            Q0=makeQuery(id+"F0.imprint","IMPRINT",FACE,{"disambiguationData":[TD([[makeQuery(id+"F0.imprint","IMPRINT",EDGE,{"derivedFrom":sQuery(id+"F0.wireOp",EDGE,"E80.MirrorCS")}),-1.0]])]});
            var Q1;
            {var subQ0=sQuery(id+"F0.wireOp",EDGE,"E145.MirrorCS");Q1=makeQuery(id+"F0.imprint","IMPRINT",FACE,{"disambiguationData":[TD([[makeQuery(id+"F0.imprint","IMPRINT",EDGE,{"derivedFrom":subQ0}),1.0]])]});}
            var Q2;
            {var subQ6=sQuery(id+"F0.wireOp",EDGE,"E121.MirrorCS");Q2=makeQuery(id+"F0.imprint","IMPRINT",FACE,{"disambiguationData":[TD([[makeQuery(id+"F0.imprint","IMPRINT",EDGE,{"derivedFrom":subQ6}),1.0]])]});}
            var Q3;
            Q3=makeQuery(id+"F0.imprint","IMPRINT",FACE,{"disambiguationData":[TD([[makeQuery(id+"F0.imprint","IMPRINT",EDGE,{"derivedFrom":sQuery(id+"F0.wireOp",EDGE,"E0")}),-1.0]])]});
            var Q4;
            Q4=makeQuery(id+"F0.imprint","IMPRINT",FACE,{"disambiguationData":[TD([[makeQuery(id+"F0.imprint","IMPRINT",EDGE,{"derivedFrom":sQuery(id+"F0.wireOp",EDGE,"E28.MirrorCS")}),-1.0]])]});
            extrude(context, id + "F2", {"entities" : qUnion([Q0, Q1, Q2, Q3, Q4]), "depth" : 1700 * mm, "offsetDistance" : 25 * mm});
        }
        {
            var Q0;
            Q0=makeQuery(id+"F2.opExtrude","CAP_FACE",FACE,{"disambiguationData":[OSD([sQuery(id+"F0.wireOp",EDGE,"E145.MirrorCS"),sQuery(id+"F0.wireOp",EDGE,"E151.MirrorCS"),sQuery(id+"F0.wireOp",EDGE,"E156.MirrorCS"),sQuery(id+"F0.wireOp",EDGE,"E160.MirrorCS"),sQuery(id+"F0.wireOp",EDGE,"E164.MirrorCS"),sQuery(id+"F0.wireOp",EDGE,"E167.MirrorCS"),sQuery(id+"F0.wireOp",EDGE,"E168.MirrorCS"),sQuery(id+"F0.wireOp",EDGE,"E172.MirrorCS"),sQuery(id+"F0.wireOp",EDGE,"E173.MirrorCS"),sQuery(id+"F0.wireOp",EDGE,"E178.MirrorCS"),sQuery(id+"F0.wireOp",EDGE,"E180.MirrorCS"),sQuery(id+"F0.wireOp",EDGE,"E184.MirrorCS"),sQuery(id+"F0.wireOp",EDGE,"E185.MirrorCS"),sQuery(id+"F0.wireOp",EDGE,"E189.MirrorCS"),sQuery(id+"F0.wireOp",EDGE,"E192.MirrorCS"),sQuery(id+"F0.wireOp",EDGE,"E194.MirrorCS"),sQuery(id+"F0.wireOp",EDGE,"E195.MirrorCS"),sQuery(id+"F0.wireOp",EDGE,"E197.MirrorCS"),sQuery(id+"F0.wireOp",EDGE,"E199.MirrorCS"),sQuery(id+"F0.wireOp",EDGE,"E200.MirrorCS"),sQuery(id+"F0.wireOp",EDGE,"E209.MirrorCS"),sQuery(id+"F0.wireOp",EDGE,"E211.MirrorCS"),sQuery(id+"F0.wireOp",EDGE,"E212.MirrorCS"),sQuery(id+"F0.wireOp",EDGE,"E213.MirrorCS"),sQuery(id+"F0.wireOp",EDGE,"E217.MirrorCS"),sQuery(id+"F0.wireOp",EDGE,"E219.MirrorCS"),sQuery(id+"F0.wireOp",EDGE,"E221.MirrorCS"),sQuery(id+"F0.wireOp",EDGE,"E227.MirrorCS"),sQuery(id+"F0.wireOp",EDGE,"E263.MirrorCS"),sQuery(id+"F0.wireOp",EDGE,"E271.MirrorCS"),sQuery(id+"F0.wireOp",EDGE,"E272.MirrorCS"),sQuery(id+"F0.wireOp",EDGE,"E273.MirrorCS"),sQuery(id+"F0.wireOp",EDGE,"E274.MirrorCS"),sQuery(id+"F0.wireOp",EDGE,"E276.MirrorCS"),sQuery(id+"F0.wireOp",EDGE,"E279.MirrorCS"),sQuery(id+"F0.wireOp",EDGE,"E280.MirrorCS"),sQuery(id+"F0.wireOp",EDGE,"E281.MirrorCS"),sQuery(id+"F0.wireOp",EDGE,"E283.MirrorCS")])],"isStart":true});
            var sketch = newSketch(context, id + "F3", { "sketchPlane" : qUnion([Q0])});
            skLineSegment(sketch, "E291", {"start": v(-444, 188.1) * mm, "end": v(-416.02, 216.07) * mm});
            skLineSegment(sketch, "E292", {"start": v(-444, 188.1) * mm, "end": v(-444, -188.1) * mm});
            skLineSegment(sketch, "E293", {"start": v(-444, -188.1) * mm, "end": v(-416.1, -216) * mm});
            skLineSegment(sketch, "E294", {"start": v(-416.1, -216) * mm, "end": v(416.1, -216) * mm});
            skLineSegment(sketch, "E295", {"start": v(416.1, -216) * mm, "end": v(444, -188.1) * mm});
            skLineSegment(sketch, "E296", {"start": v(444, -188.1) * mm, "end": v(444, 188.1) * mm});
            skLineSegment(sketch, "E297", {"start": v(444, 188.1) * mm, "end": v(416.3, 215.78) * mm});
            skLineSegment(sketch, "E298", {"start": v(-416.02, 216.07) * mm, "end": v(416.3, 215.78) * mm});
            skSolve(sketch);
        }
        {
            var Q0;
            Q0 = qSketchRegion(id + "F3", true);
            extrude(context, id + "F4", {"entities" : qUnion([Q0]), "oppositeDirection" : true, "depth" : 19 * mm, "offsetDistance" : 25 * mm});
        }
        {
            var Q0;
            Q0=makeQuery(id+"F4.opExtrude","SWEPT_BODY",BODY,{"disambiguationData":[OSD([sQuery(id+"F3.wireOp",EDGE,"JyY8OK89-OxwZ-t4ao-3A1r-hap6NcHj4FOZ"),sQuery(id+"F3.wireOp",EDGE,"E291"),sQuery(id+"F3.wireOp",EDGE,"E292"),sQuery(id+"F3.wireOp",EDGE,"E293"),sQuery(id+"F3.wireOp",EDGE,"E294"),sQuery(id+"F3.wireOp",EDGE,"E295"),sQuery(id+"F3.wireOp",EDGE,"E296"),sQuery(id+"F3.wireOp",EDGE,"E297")])]});
            var Q1;
            Q1=makeQuery(id+"F1.opExtrude","SWEPT_EDGE",EDGE,{"disambiguationData":[OSD([sQuery(id+"F0.wireOp",EDGE,"E132.MirrorCS"),sQuery(id+"F0.wireOp",EDGE,"E228.MirrorCS")])]});
            var Q2;
            Q2=makeQuery(id+"F2.opExtrude","SWEPT_EDGE",EDGE,{"disambiguationData":[OSD([sQuery(id+"F0.wireOp",EDGE,"E227.MirrorCS"),sQuery(id+"F0.wireOp",EDGE,"E280.MirrorCS")])]});
            transform(context, id + "F5", {"entities" : qUnion([Q0]), "transformType" : TransformType.TRANSLATION_DISTANCE, "transformDirection" : qUnion([Q2]), "distance" : 1681 * mm, "oppositeDirection" : true, "makeCopy" : true});
        }
        {
            var Q0;
            Q0=makeQuery(id+"F4.opExtrude","CAP_FACE",FACE,{"disambiguationData":[OSD([sQuery(id+"F3.wireOp",EDGE,"JyY8OK89-OxwZ-t4ao-3A1r-hap6NcHj4FOZ"),sQuery(id+"F3.wireOp",EDGE,"E291"),sQuery(id+"F3.wireOp",EDGE,"E292"),sQuery(id+"F3.wireOp",EDGE,"E293"),sQuery(id+"F3.wireOp",EDGE,"E294"),sQuery(id+"F3.wireOp",EDGE,"E295"),sQuery(id+"F3.wireOp",EDGE,"E296"),sQuery(id+"F3.wireOp",EDGE,"E297")])],"isStart":true});
            var sketch = newSketch(context, id + "F6", { "sketchPlane" : qUnion([Q0])});
            skLineSegment(sketch, "E299", {"start": v(-210.32, 0) * mm, "end": v(-421.2, 210.88) * mm});
            skLineSegment(sketch, "E300", {"start": v(-421.2, 210.88) * mm, "end": v(-438.88, 193.2) * mm});
            skLineSegment(sketch, "E301", {"start": v(0, 0) * mm, "end": v(-210.32, 0) * mm, "construction": true});
            skLineSegment(sketch, "E302", {"start": v(0, 0) * mm, "end": v(0, -107.84) * mm, "construction": true});
            skLineSegment(sketch, "E303.MirrorCS", {"start": v(-421.2, -210.88) * mm, "end": v(-438.88, -193.2) * mm});
            skLineSegment(sketch, "E304.MirrorCS", {"start": v(421.2, -210.88) * mm, "end": v(438.88, -193.2) * mm});
            skLineSegment(sketch, "E305.MirrorCS", {"start": v(421.2, 210.88) * mm, "end": v(438.88, 193.2) * mm});
            skLineSegment(sketch, "E306", {"start": v(-438.88, 193.2) * mm, "end": v(-228, -17.68) * mm});
            skLineSegment(sketch, "E307", {"start": v(-210.32, 0) * mm, "end": v(-228, -17.68) * mm});
            skLineSegment(sketch, "E308", {"start": v(-438.88, -193.2) * mm, "end": v(-245.68, 0) * mm});
            skLineSegment(sketch, "E309", {"start": v(-245.68, 0) * mm, "end": v(-228, -17.68) * mm});
            skLineSegment(sketch, "E310", {"start": v(-228, -17.68) * mm, "end": v(-421.2, -210.88) * mm});
            skLineSegment(sketch, "E311.MirrorCS", {"start": v(210.32, 0) * mm, "end": v(228, -17.68) * mm});
            skLineSegment(sketch, "E312.MirrorCS", {"start": v(210.32, 0) * mm, "end": v(421.2, 210.88) * mm});
            skLineSegment(sketch, "E313.MirrorCS", {"start": v(438.88, 193.2) * mm, "end": v(228, -17.68) * mm});
            skLineSegment(sketch, "E314.MirrorCS", {"start": v(245.68, 0) * mm, "end": v(228, -17.68) * mm});
            skLineSegment(sketch, "E315.MirrorCS", {"start": v(438.88, -193.2) * mm, "end": v(245.68, 0) * mm});
            skLineSegment(sketch, "E316.MirrorCS", {"start": v(228, -17.68) * mm, "end": v(421.2, -210.88) * mm});
            skSolve(sketch);
        }
        {
            var Q0;
            {var subQ0=sQuery(id+"F6.wireOp",EDGE,"E309");Q0=makeQuery(id+"F6.imprint","IMPRINT",FACE,{"disambiguationData":[TD([[makeQuery(id+"F6.imprint","IMPRINT",EDGE,{"derivedFrom":subQ0}),-1.0]])]});}
            var Q1;
            {var subQ0=sQuery(id+"F6.wireOp",EDGE,"E314.MirrorCS");Q1=makeQuery(id+"F6.imprint","IMPRINT",FACE,{"disambiguationData":[TD([[makeQuery(id+"F6.imprint","IMPRINT",EDGE,{"derivedFrom":subQ0}),1.0]])]});}
            var Q2;
            {var subQ0=sQuery(id+"F6.wireOp",EDGE,"E304.MirrorCS");Q2=makeQuery(id+"F6.imprint","IMPRINT",FACE,{"disambiguationData":[TD([[makeQuery(id+"F6.imprint","IMPRINT",EDGE,{"derivedFrom":subQ0}),1.0]])]});}
            var Q3;
            {var subQ0=sQuery(id+"F6.wireOp",EDGE,"E303.MirrorCS");Q3=makeQuery(id+"F6.imprint","IMPRINT",FACE,{"disambiguationData":[TD([[makeQuery(id+"F6.imprint","IMPRINT",EDGE,{"derivedFrom":subQ0}),-1.0]])]});}
            extrude(context, id + "F7", {"entities" : qUnion([Q0, Q1, Q2, Q3]), "depth" : 40 * mm, "offsetDistance" : 25 * mm});
        }
        {
            var Q0;
            {var subQ4=sQuery(id+"F6.wireOp",EDGE,"E307");Q0=makeQuery(id+"F6.imprint","IMPRINT",FACE,{"disambiguationData":[TD([[makeQuery(id+"F6.imprint","IMPRINT",EDGE,{"derivedFrom":subQ4}),-1.0]])]});}
            var Q1;
            {var subQ5=sQuery(id+"F6.wireOp",EDGE,"E311.MirrorCS");Q1=makeQuery(id+"F6.imprint","IMPRINT",FACE,{"disambiguationData":[TD([[makeQuery(id+"F6.imprint","IMPRINT",EDGE,{"derivedFrom":subQ5}),1.0]])]});}
            var Q2;
            {var subQ0=sQuery(id+"F6.wireOp",EDGE,"E300");Q2=makeQuery(id+"F6.imprint","IMPRINT",FACE,{"disambiguationData":[TD([[makeQuery(id+"F6.imprint","IMPRINT",EDGE,{"derivedFrom":subQ0}),1.0]])]});}
            var Q3;
            {var subQ0=sQuery(id+"F6.wireOp",EDGE,"E305.MirrorCS");Q3=makeQuery(id+"F6.imprint","IMPRINT",FACE,{"disambiguationData":[TD([[makeQuery(id+"F6.imprint","IMPRINT",EDGE,{"derivedFrom":subQ0}),-1.0]])]});}
            var Q4;
            Q4=makeQuery(id+"F7.opExtrude","CAP_FACE",FACE,{"disambiguationData":[OSD([sQuery(id+"F3.wireOp",EDGE,"E293"),sQuery(id+"F6.wireOp",EDGE,"E308"),sQuery(id+"F6.wireOp",EDGE,"E309"),sQuery(id+"F6.wireOp",EDGE,"E310")])],"isStart":false});
            extrude(context, id + "F8", {"entities" : qUnion([Q0, Q1, Q2, Q3]), "endBound" : BoundingType.UP_TO_SURFACE, "depth" : 40 * mm, "endBoundEntityFace" : qUnion([Q4]), "offsetDistance" : 25 * mm});
        }
        {
            var Q0;
            Q0=makeQuery(id+"F7.opExtrude","SWEPT_BODY",BODY,{"disambiguationData":[OSD([sQuery(id+"F3.wireOp",EDGE,"E295"),sQuery(id+"F6.wireOp",EDGE,"E314.MirrorCS"),sQuery(id+"F6.wireOp",EDGE,"E315.MirrorCS"),sQuery(id+"F6.wireOp",EDGE,"E316.MirrorCS")])]});
            var Q1;
            Q1=makeQuery(id+"F8.opExtrude","SWEPT_BODY",BODY,{"disambiguationData":[OSD([sQuery(id+"F3.wireOp",EDGE,"E297"),sQuery(id+"F6.wireOp",EDGE,"E311.MirrorCS"),sQuery(id+"F6.wireOp",EDGE,"E312.MirrorCS"),sQuery(id+"F6.wireOp",EDGE,"E313.MirrorCS"),sQuery(id+"F6.wireOp",EDGE,"E314.MirrorCS")])]});
            var Q2;
            Q2=makeQuery(id+"F7.opExtrude","SWEPT_BODY",BODY,{"disambiguationData":[OSD([sQuery(id+"F3.wireOp",EDGE,"E293"),sQuery(id+"F6.wireOp",EDGE,"E308"),sQuery(id+"F6.wireOp",EDGE,"E309"),sQuery(id+"F6.wireOp",EDGE,"E310")])]});
            var Q3;
            Q3=makeQuery(id+"F8.opExtrude","SWEPT_BODY",BODY,{"disambiguationData":[OSD([sQuery(id+"F3.wireOp",EDGE,"E291"),sQuery(id+"F6.wireOp",EDGE,"E299"),sQuery(id+"F6.wireOp",EDGE,"E306"),sQuery(id+"F6.wireOp",EDGE,"E307"),sQuery(id+"F6.wireOp",EDGE,"E309")])]});
            var Q4;
            Q4=makeQuery(id+"F2.opExtrude","SWEPT_EDGE",EDGE,{"disambiguationData":[OSD([sQuery(id+"F0.wireOp",EDGE,"E52.MirrorCS"),sQuery(id+"F0.wireOp",EDGE,"E59.MirrorCS")])]});
            var Q5;
            Q5=makeQuery(id+"F1.opExtrude","SWEPT_EDGE",EDGE,{"disambiguationData":[OSD([sQuery(id+"F0.wireOp",EDGE,"E7.bottom"),sQuery(id+"F0.wireOp",EDGE,"E12")])]});
            transform(context, id + "F9", {"entities" : qUnion([Q0, Q1, Q2, Q3]), "transformType" : TransformType.TRANSLATION_DISTANCE, "transformDirection" : qUnion([Q5]), "distance" : 1681 * mm, "oppositeDirection" : true, "makeCopy" : true});
        }
        {
            var Q0;
            Q0=makeQuery(id+"F5.opPattern","COPY",FACE,{"derivedFrom":makeQuery(id+"F4.opExtrude","CAP_FACE",FACE,{"disambiguationData":[OSD([sQuery(id+"F3.wireOp",EDGE,"JyY8OK89-OxwZ-t4ao-3A1r-hap6NcHj4FOZ"),sQuery(id+"F3.wireOp",EDGE,"E291"),sQuery(id+"F3.wireOp",EDGE,"E292"),sQuery(id+"F3.wireOp",EDGE,"E293"),sQuery(id+"F3.wireOp",EDGE,"E294"),sQuery(id+"F3.wireOp",EDGE,"E295"),sQuery(id+"F3.wireOp",EDGE,"E296"),sQuery(id+"F3.wireOp",EDGE,"E297")])],"isStart":false}),"instanceName":"1"});
            var Q1;
            {var subQ1=sQuery(id+"F6.wireOp",EDGE,"E307");Q1=makeQuery(id+"F6.imprint","IMPRINT",FACE,{"disambiguationData":[TD([[makeQuery(id+"F6.imprint","IMPRINT",EDGE,{"derivedFrom":subQ1}),1.0]])]});}
            cPlane(context, id + "F10", {"entities" : qUnion([Q0, Q1]), "cplaneType" : CPlaneType.MID_PLANE, "offset" : 25 * mm, "width" : 150 * mm, "height" : 150 * mm});
        }
        {
            var Q0;
            Q0=qCreatedBy(id+"F10.planeOp",FACE);
            var sketch = newSketch(context, id + "F11", { "sketchPlane" : qUnion([Q0])});
            skLineSegment(sketch, "E317.0.0", {"start": v(444, -188.1) * mm, "end": v(444, 188.1) * mm});
            skLineSegment(sketch, "E317.0.1", {"start": v(444, 188.1) * mm, "end": v(416.1, 216) * mm});
            skLineSegment(sketch, "E317.0.2", {"start": v(416.1, 216) * mm, "end": v(-416.1, 216) * mm});
            skLineSegment(sketch, "E317.0.3", {"start": v(-416.1, 216) * mm, "end": v(-444, 188.1) * mm});
            skLineSegment(sketch, "E317.0.4", {"start": v(-444, 188.1) * mm, "end": v(-444, -188.1) * mm});
            skLineSegment(sketch, "E317.0.5", {"start": v(-444, -188.1) * mm, "end": v(-444, -188.1) * mm});
            skLineSegment(sketch, "E317.0.6", {"start": v(-444, -188.1) * mm, "end": v(419.8, -212.3) * mm});
            skLineSegment(sketch, "E317.0.7", {"start": v(419.8, -212.3) * mm, "end": v(444, -188.1) * mm});
            skSolve(sketch);
        }
        {
            var Q0;
            Q0 = qSketchRegion(id + "F11", true);
            extrude(context, id + "F12", {"entities" : qUnion([Q0]), "depth" : 3 * mm, "offsetDistance" : 25 * mm, "hasSecondDirection" : true, "secondDirectionOppositeDirection" : true, "secondDirectionDepth" : 3 * mm});
        }
        {
            var Q0;
            Q0=makeQuery(id+"F12.opExtrude","SWEPT_BODY",BODY,{"disambiguationData":[OSD([sQuery(id+"F11.wireOp",EDGE,"E317.0.0"),sQuery(id+"F11.wireOp",EDGE,"E317.0.1"),sQuery(id+"F11.wireOp",EDGE,"E317.0.2"),sQuery(id+"F11.wireOp",EDGE,"E317.0.3"),sQuery(id+"F11.wireOp",EDGE,"E317.0.4"),sQuery(id+"F11.wireOp",EDGE,"E317.0.5"),sQuery(id+"F11.wireOp",EDGE,"E317.0.6"),sQuery(id+"F11.wireOp",EDGE,"E317.0.7")])]});
            transform(context, id + "F13", {"entities" : qUnion([Q0]), "transformType" : TransformType.TRANSLATION_3D, "dx" : 0 * mm, "dy" : 0 * mm, "dz" : 360 * mm, "makeCopy" : true});
        }
        {
            var Q0;
            Q0=makeQuery(id+"F12.opExtrude","SWEPT_BODY",BODY,{"disambiguationData":[OSD([sQuery(id+"F11.wireOp",EDGE,"E317.0.0"),sQuery(id+"F11.wireOp",EDGE,"E317.0.1"),sQuery(id+"F11.wireOp",EDGE,"E317.0.2"),sQuery(id+"F11.wireOp",EDGE,"E317.0.3"),sQuery(id+"F11.wireOp",EDGE,"E317.0.4"),sQuery(id+"F11.wireOp",EDGE,"E317.0.5"),sQuery(id+"F11.wireOp",EDGE,"E317.0.6"),sQuery(id+"F11.wireOp",EDGE,"E317.0.7")])]});
            transform(context, id + "F14", {"entities" : qUnion([Q0]), "transformType" : TransformType.TRANSLATION_3D, "dx" : 0 * mm, "dy" : 0 * mm, "dz" : -360 * mm, "makeCopy" : true});
        }
        {
            var Q0;
            Q0=makeQuery(id+"F1.opExtrude","SWEPT_FACE",FACE,{"disambiguationData":[OSD([sQuery(id+"F0.wireOp",EDGE,"E126.MirrorCS")])]});
            var sketch = newSketch(context, id + "F15", { "sketchPlane" : qUnion([Q0])});
            skCircle(sketch, "E318", {"center": v(461.85, 100) * mm, "radius": 2 * mm});
            skCircle(sketch, "E319", {"center": v(461.85, 1600) * mm, "radius": 2 * mm});
            skSolve(sketch);
        }
        {
            var Q0;
            Q0=makeQuery(id+"F15.imprint","IMPRINT",FACE,{"disambiguationData":[TD([[makeQuery(id+"F15.imprint","IMPRINT",EDGE,{"derivedFrom":sQuery(id+"F15.wireOp",EDGE,"E319")}),1.0]])]});
            var Q1;
            Q1=makeQuery(id+"F15.imprint","IMPRINT",FACE,{"disambiguationData":[TD([[makeQuery(id+"F15.imprint","IMPRINT",EDGE,{"derivedFrom":sQuery(id+"F15.wireOp",EDGE,"E318")}),1.0]])]});
            extrude(context, id + "F16", {"entities" : qUnion([Q0, Q1]), "operationType" : NewBodyOperationType.REMOVE, "endBound" : BoundingType.THROUGH_ALL, "oppositeDirection" : true, "depth" : 25 * mm, "offsetDistance" : 25 * mm, "hasSecondDirection" : true, "secondDirectionBound" : SecondDirectionBoundingType.THROUGH_ALL, "secondDirectionOppositeDirection" : false, "secondDirectionDepth" : 25 * mm});
        }
    });
